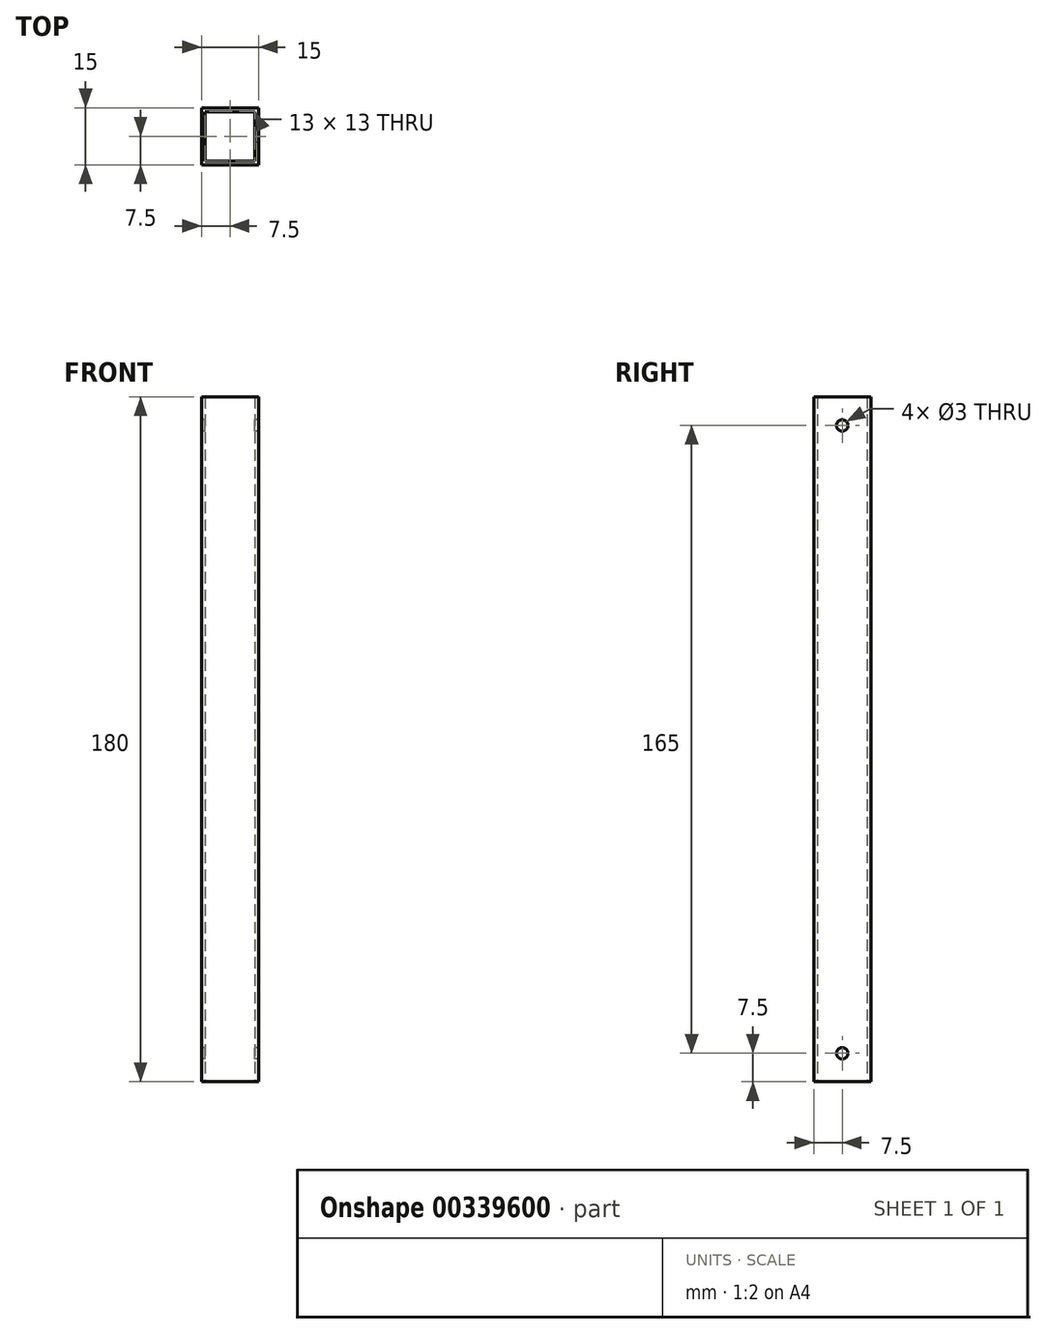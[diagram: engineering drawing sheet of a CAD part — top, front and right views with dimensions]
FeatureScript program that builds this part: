
annotation { "Feature Type Name" : "Feature", "Feature Type Description" : "" }
export const myFeature = defineFeature(function(context is Context, id is Id, definition is map)
    precondition{}
    {
        {
            var Q0;
            Q0=qCreatedBy(makeId("Top.planeOp"),FACE);
            var sketch = newSketch(context, id + "F0", { "sketchPlane" : qUnion([Q0])});
            skLineSegment(sketch, "E0.bottom", {"start": v(-7.5, 7.5) * mm, "end": v(7.5, 7.5) * mm});
            skLineSegment(sketch, "E0.top", {"start": v(-7.5, -7.5) * mm, "end": v(7.5, -7.5) * mm});
            skLineSegment(sketch, "E0.left", {"start": v(-7.5, 7.5) * mm, "end": v(-7.5, -7.5) * mm});
            skLineSegment(sketch, "E0.right", {"start": v(7.5, 7.5) * mm, "end": v(7.5, -7.5) * mm});
            skLineSegment(sketch, "E1.bottom", {"start": v(-6.5, 6.5) * mm, "end": v(6.5, 6.5) * mm});
            skLineSegment(sketch, "E1.top", {"start": v(-6.5, -6.5) * mm, "end": v(6.5, -6.5) * mm});
            skLineSegment(sketch, "E1.left", {"start": v(-6.5, 6.5) * mm, "end": v(-6.5, -6.5) * mm});
            skLineSegment(sketch, "E1.right", {"start": v(6.5, 6.5) * mm, "end": v(6.5, -6.5) * mm});
            skLineSegment(sketch, "E2", {"start": v(-7.5, 7.5) * mm, "end": v(-6.5, 6.5) * mm});
            skLineSegment(sketch, "E3", {"start": v(6.5, -6.5) * mm, "end": v(7.5, -7.5) * mm});
            skLineSegment(sketch, "E4", {"start": v(-6.5, 6.5) * mm, "end": v(6.5, -6.5) * mm});
            skPoint(sketch, "E5", {"position": v(0, 0) * mm});
            skSolve(sketch);
        }
        {
            var Q0;
            Q0=makeQuery(id+"F0.imprint","IMPRINT",FACE,{"disambiguationData":[TD([[makeQuery(id+"F0.imprint","IMPRINT",EDGE,{"derivedFrom":sQuery(id+"F0.wireOp",EDGE,"E0.top")}),1.0]])]});
            var Q1;
            Q1=makeQuery(id+"F0.imprint","IMPRINT",FACE,{"disambiguationData":[TD([[makeQuery(id+"F0.imprint","IMPRINT",EDGE,{"derivedFrom":sQuery(id+"F0.wireOp",EDGE,"E0.bottom")}),-1.0]])]});
            extrude(context, id + "F1", {"entities" : qUnion([Q0, Q1]), "endBound" : BoundingType.SYMMETRIC, "depth" : 180 * mm});
        }
        {
            var Q0;
            Q0=makeQuery(id+"F1.opExtrude","SWEPT_FACE",FACE,{"disambiguationData":[OSD([sQuery(id+"F0.wireOp",EDGE,"E0.left")])]});
            var sketch = newSketch(context, id + "F2", { "sketchPlane" : qUnion([Q0])});
            skLineSegment(sketch, "E6.bottom", {"start": v(-7.5, 90) * mm, "end": v(7.5, 90) * mm});
            skLineSegment(sketch, "E6.top", {"start": v(-7.5, 75) * mm, "end": v(7.5, 75) * mm});
            skLineSegment(sketch, "E6.left", {"start": v(-7.5, 90) * mm, "end": v(-7.5, 75) * mm});
            skLineSegment(sketch, "E6.right", {"start": v(7.5, 90) * mm, "end": v(7.5, 75) * mm});
            skLineSegment(sketch, "E7.bottom", {"start": v(-7.5, -90) * mm, "end": v(7.5, -90) * mm});
            skLineSegment(sketch, "E7.top", {"start": v(-7.5, -75) * mm, "end": v(7.5, -75) * mm});
            skLineSegment(sketch, "E7.left", {"start": v(-7.5, -90) * mm, "end": v(-7.5, -75) * mm});
            skLineSegment(sketch, "E7.right", {"start": v(7.5, -90) * mm, "end": v(7.5, -75) * mm});
            skLineSegment(sketch, "E8", {"start": v(-7.5, 90) * mm, "end": v(7.5, 75) * mm});
            skLineSegment(sketch, "E9", {"start": v(-7.5, -75) * mm, "end": v(7.5, -90) * mm});
            skPoint(sketch, "E10", {"position": v(0, -82.5) * mm});
            skPoint(sketch, "E11", {"position": v(0, 82.5) * mm});
            skSolve(sketch);
        }
        {
            var Q0;
            Q0=sQuery(id+"F2.wireOp",VERTEX,"E11");
            var Q1;
            Q1=sQuery(id+"F2.wireOp",VERTEX,"E10");
            var Q2;
            Q2=makeQuery(id+"F1.opExtrude","SWEPT_BODY",BODY,{"disambiguationData":[OSD([sQuery(id+"F0.wireOp",EDGE,"E0.bottom"),sQuery(id+"F0.wireOp",EDGE,"E0.top"),sQuery(id+"F0.wireOp",EDGE,"E0.left"),sQuery(id+"F0.wireOp",EDGE,"E0.right"),sQuery(id+"F0.wireOp",EDGE,"E1.bottom"),sQuery(id+"F0.wireOp",EDGE,"E1.top"),sQuery(id+"F0.wireOp",EDGE,"E1.left"),sQuery(id+"F0.wireOp",EDGE,"E1.right")])]});
            hole(context, id + "F3", {"style" : HoleStyle.SIMPLE, "holeDiameter" : 3 * mm, "endStyle" : HoleEndStyle.THROUGH, "locations" : qUnion([Q0, Q1]), "scope" : qUnion([Q2])});
        }
    });
